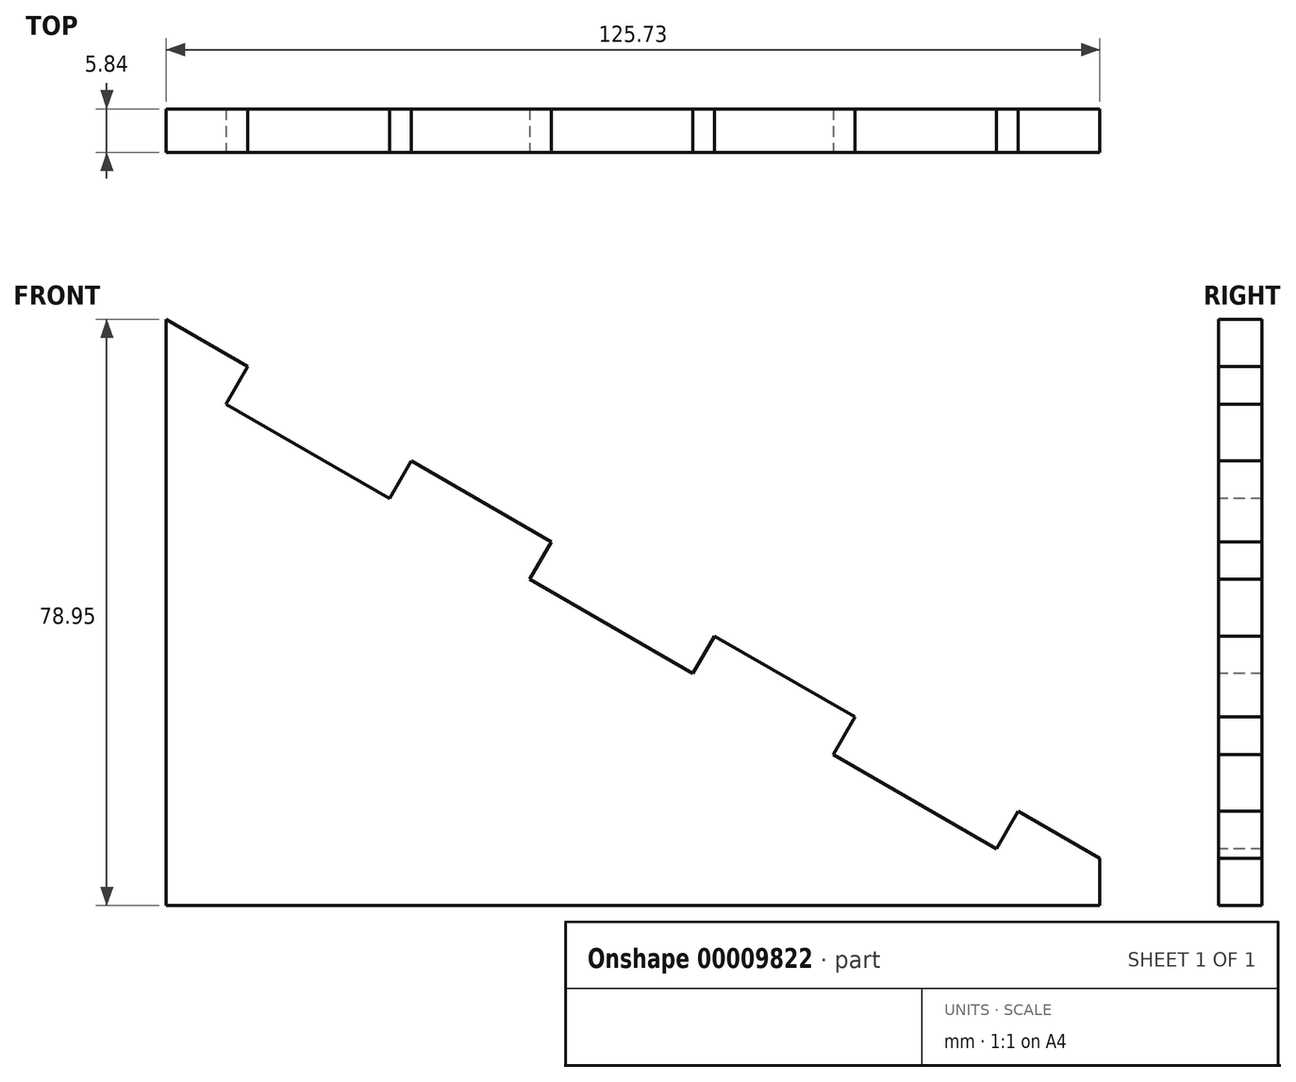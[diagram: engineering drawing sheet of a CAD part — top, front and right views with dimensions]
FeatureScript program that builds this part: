
annotation { "Feature Type Name" : "Feature", "Feature Type Description" : "" }
export const myFeature = defineFeature(function(context is Context, id is Id, definition is map)
    precondition{}
    {
        {
            var Q0;
            Q0=qCreatedBy(makeId("Front.planeOp"),FACE);
            var sketch = newSketch(context, id + "F0", { "sketchPlane" : qUnion([Q0])});
            skLineSegment(sketch, "E0", {"start": v(-45.34, 45.87) * mm, "end": v(-34.34, 39.52) * mm});
            skLineSegment(sketch, "E1", {"start": v(-34.34, 39.52) * mm, "end": v(-37.27, 34.46) * mm});
            skLineSegment(sketch, "E2", {"start": v(-37.27, 34.46) * mm, "end": v(-15.27, 21.76) * mm});
            skLineSegment(sketch, "E3", {"start": v(-15.27, 21.76) * mm, "end": v(-12.35, 26.82) * mm});
            skLineSegment(sketch, "E4", {"start": v(-12.35, 26.82) * mm, "end": v(6.53, 15.92) * mm});
            skLineSegment(sketch, "E5", {"start": v(6.53, 15.92) * mm, "end": v(3.6, 10.86) * mm});
            skLineSegment(sketch, "E6", {"start": v(3.6, 10.86) * mm, "end": v(25.6, -1.84) * mm});
            skLineSegment(sketch, "E7", {"start": v(25.6, -1.84) * mm, "end": v(28.52, 3.22) * mm});
            skLineSegment(sketch, "E8", {"start": v(28.52, 3.22) * mm, "end": v(47.4, -7.68) * mm});
            skLineSegment(sketch, "E9", {"start": v(47.4, -7.68) * mm, "end": v(44.48, -12.73) * mm});
            skLineSegment(sketch, "E10", {"start": v(44.48, -12.73) * mm, "end": v(66.47, -25.43) * mm});
            skLineSegment(sketch, "E11", {"start": v(66.47, -25.43) * mm, "end": v(69.4, -20.38) * mm});
            skLineSegment(sketch, "E12", {"start": v(69.4, -20.38) * mm, "end": v(80.4, -26.73) * mm});
            skPoint(sketch, "E13", {"position": v(14.6, 4.51) * mm});
            skLineSegment(sketch, "E14", {"start": v(-45.34, 45.87) * mm, "end": v(-33.91, 65.67) * mm, "construction": true});
            skLineSegment(sketch, "E15", {"start": v(80.4, -26.73) * mm, "end": v(91.82, -6.93) * mm, "construction": true});
            skLineSegment(sketch, "E16", {"start": v(-33.91, 65.67) * mm, "end": v(91.82, -6.93) * mm, "construction": true});
            skPoint(sketch, "E17", {"position": v(28.96, 29.37) * mm});
            skLineSegment(sketch, "E18", {"start": v(28.96, 29.37) * mm, "end": v(14.6, 4.51) * mm, "construction": true});
            skLineSegment(sketch, "E19", {"start": v(-45.34, 45.87) * mm, "end": v(-45.34, -33.08) * mm});
            skLineSegment(sketch, "E20", {"start": v(-45.34, -33.08) * mm, "end": v(80.4, -33.08) * mm});
            skLineSegment(sketch, "E21", {"start": v(80.4, -33.08) * mm, "end": v(80.4, -26.73) * mm});
            skLineSegment(sketch, "E22.bottom", {"start": v(-32.64, -33.08) * mm, "end": v(-7.24, -33.08) * mm});
            skLineSegment(sketch, "E22.top", {"start": v(-32.64, -38.92) * mm, "end": v(-7.24, -38.92) * mm});
            skLineSegment(sketch, "E22.left", {"start": v(-32.64, -38.92) * mm, "end": v(-32.64, -33.08) * mm});
            skLineSegment(sketch, "E22.right", {"start": v(-7.24, -38.92) * mm, "end": v(-7.24, -33.08) * mm});
            skLineSegment(sketch, "E23.bottom", {"start": v(42.3, -33.08) * mm, "end": v(67.7, -33.08) * mm});
            skLineSegment(sketch, "E23.top", {"start": v(42.3, -38.92) * mm, "end": v(67.7, -38.92) * mm});
            skLineSegment(sketch, "E23.left", {"start": v(42.3, -38.92) * mm, "end": v(42.3, -33.08) * mm});
            skLineSegment(sketch, "E23.right", {"start": v(67.7, -38.92) * mm, "end": v(67.7, -33.08) * mm});
            skSolve(sketch);
        }
        {
            var Q0;
            Q0=makeQuery(id+"F0.imprint","IMPRINT",FACE,{"disambiguationData":[TD([[makeQuery(id+"F0.imprint","IMPRINT",EDGE,{"derivedFrom":sQuery(id+"F0.wireOp",EDGE,"E0")}),-1.0]])]});
            var Q1;
            Q1=makeQuery(id+"F0.imprint","IMPRINT",FACE,{"disambiguationData":[TD([[makeQuery(id+"F0.imprint","IMPRINT",EDGE,{"derivedFrom":sQuery(id+"F0.wireOp",EDGE,"E22.bottom")}),-1.0]])]});
            var Q2;
            Q2=makeQuery(id+"F0.imprint","IMPRINT",FACE,{"disambiguationData":[TD([[makeQuery(id+"F0.imprint","IMPRINT",EDGE,{"derivedFrom":sQuery(id+"F0.wireOp",EDGE,"E23.bottom")}),-1.0]])]});
            extrude(context, id + "F1", {"entities" : qUnion([Q0, Q1, Q2]), "oppositeDirection" : true, "depth" : 5.84 * mm});
        }
    });
